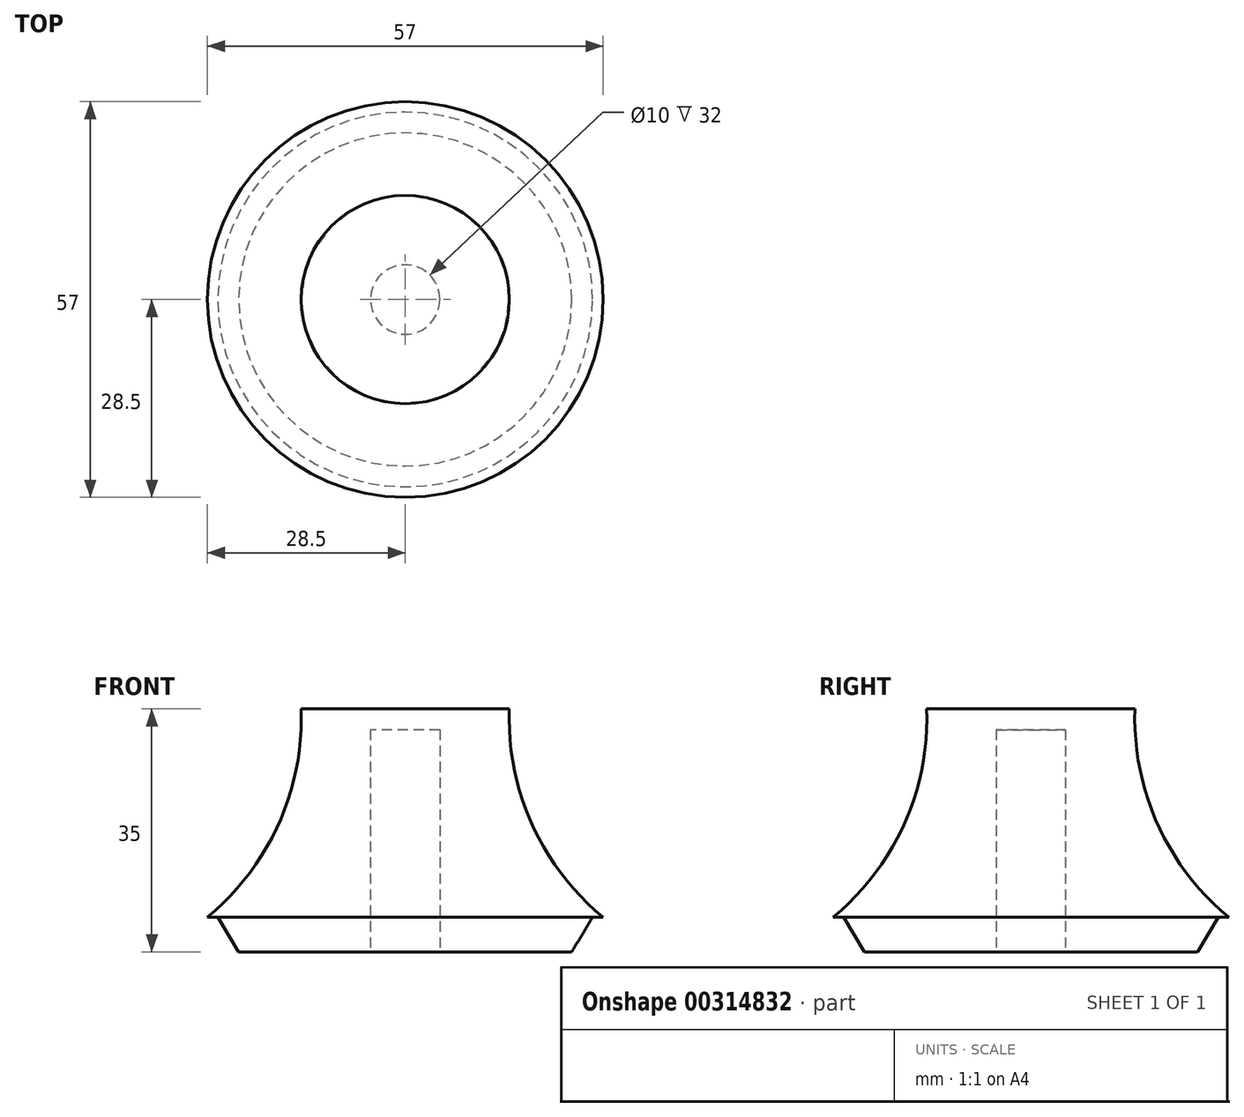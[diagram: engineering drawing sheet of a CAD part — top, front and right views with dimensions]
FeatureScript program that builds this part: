
annotation { "Feature Type Name" : "Feature", "Feature Type Description" : "" }
export const myFeature = defineFeature(function(context is Context, id is Id, definition is map)
    precondition{}
    {
        {
            var Q0;
            Q0=qCreatedBy(makeId("Front.planeOp"),FACE);
            var sketch = newSketch(context, id + "F0", { "sketchPlane" : qUnion([Q0])});
            skLineSegment(sketch, "E0", {"start": v(0, 0) * mm, "end": v(24, 0) * mm});
            skLineSegment(sketch, "E1", {"start": v(27, 5) * mm, "end": v(24, 0) * mm});
            skLineSegment(sketch, "E2", {"start": v(27, 5) * mm, "end": v(28.5, 5) * mm});
            skArc(sketch, "E3", {"start": v(15, 35) * mm, "mid": v(18.24, 18.42) * mm, "end": v(28.5, 5) * mm});
            skLineSegment(sketch, "E4", {"start": v(15, 35) * mm, "end": v(0, 35) * mm});
            skLineSegment(sketch, "E5", {"start": v(0, 35) * mm, "end": v(0, 0) * mm});
            skSolve(sketch);
        }
        {
            var Q0;
            Q0 = qSketchRegion(id + "F0", true);
            var Q1;
            Q1=sQuery(id+"F0.wireOp",EDGE,"E5");
            revolve(context, id + "F1", {"entities" : qUnion([Q0]), "axis" : qUnion([Q1]), "revolveType" : RevolveType.FULL});
        }
        {
            var Q0;
            Q0=qCreatedBy(makeId("Top.planeOp"),FACE);
            var sketch = newSketch(context, id + "F2", { "sketchPlane" : qUnion([Q0])});
            skCircle(sketch, "E6", {"center": v(0, 0) * mm, "radius": 5 * mm});
            skSolve(sketch);
        }
        {
            var Q0;
            Q0 = qSketchRegion(id + "F2", true);
            extrude(context, id + "F3", {"entities" : qUnion([Q0]), "depth" : 32 * mm});
        }
        {
            var Q0;
            Q0=makeQuery(id+"F3.opExtrude","SWEPT_BODY",BODY,{"disambiguationData":[OSD([sQuery(id+"F2.wireOp",EDGE,"E6")])]});
            var Q1;
            Q1=makeQuery(id+"F1.opRevolve","SWEPT_BODY",BODY,{"disambiguationData":[OSD([sQuery(id+"F0.wireOp",EDGE,"E0"),sQuery(id+"F0.wireOp",EDGE,"E1"),sQuery(id+"F0.wireOp",EDGE,"E2"),sQuery(id+"F0.wireOp",EDGE,"E3"),sQuery(id+"F0.wireOp",EDGE,"E4"),sQuery(id+"F0.wireOp",EDGE,"E5")])]});
            booleanBodies(context, id + "F4", {"operationType" : BooleanOperationType.SUBTRACTION, "tools" : qUnion([Q0]), "targets" : qUnion([Q1])});
        }
    });
